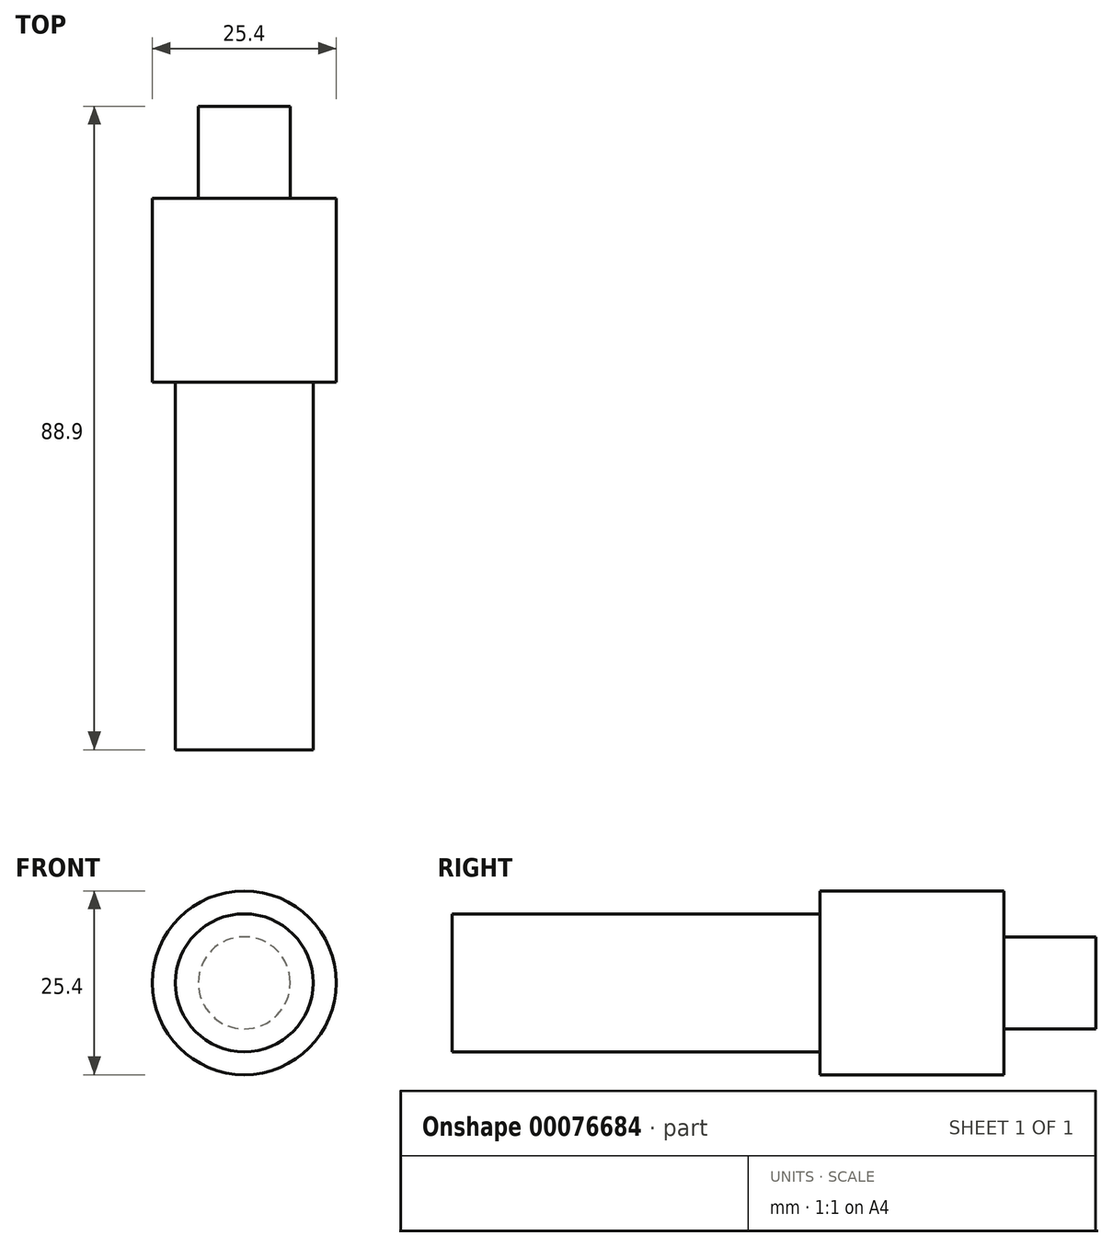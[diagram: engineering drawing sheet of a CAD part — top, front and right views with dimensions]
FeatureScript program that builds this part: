
annotation { "Feature Type Name" : "Feature", "Feature Type Description" : "" }
export const myFeature = defineFeature(function(context is Context, id is Id, definition is map)
    precondition{}
    {
        {
            var Q0;
            Q0=qCreatedBy(makeId("Front.planeOp"),FACE);
            var sketch = newSketch(context, id + "F0", { "sketchPlane" : qUnion([Q0])});
            skCircle(sketch, "E0", {"center": v(0, 0) * mm, "radius": 12.7 * mm});
            skSolve(sketch);
        }
        {
            var Q0;
            Q0=makeQuery(id+"F0.imprint","IMPRINT",FACE,{"disambiguationData":[TD([[makeQuery(id+"F0.imprint","IMPRINT",EDGE,{"derivedFrom":sQuery(id+"F0.wireOp",EDGE,"E0")}),1.0]])]});
            extrude(context, id + "F1", {"entities" : qUnion([Q0]), "depth" : 25.4 * mm});
        }
        {
            var Q0;
            Q0=makeQuery(id+"F1.opExtrude","CAP_FACE",FACE,{"disambiguationData":[OSD([sQuery(id+"F0.wireOp",EDGE,"E0")])],"isStart":true});
            var sketch = newSketch(context, id + "F2", { "sketchPlane" : qUnion([Q0])});
            skCircle(sketch, "E1", {"center": v(0, 0) * mm, "radius": 6.35 * mm});
            skSolve(sketch);
        }
        {
            var Q0;
            Q0=makeQuery(id+"F2.imprint","IMPRINT",FACE,{"disambiguationData":[TD([[makeQuery(id+"F2.imprint","IMPRINT",EDGE,{"derivedFrom":sQuery(id+"F2.wireOp",EDGE,"E1")}),1.0]])]});
            extrude(context, id + "F3", {"entities" : qUnion([Q0]), "operationType" : NewBodyOperationType.ADD, "depth" : 12.7 * mm});
        }
        {
            var Q0;
            Q0=makeQuery(id+"F1.opExtrude","CAP_FACE",FACE,{"disambiguationData":[OSD([sQuery(id+"F0.wireOp",EDGE,"E0")])],"isStart":false});
            var sketch = newSketch(context, id + "F4", { "sketchPlane" : qUnion([Q0])});
            skCircle(sketch, "E2", {"center": v(0, 0) * mm, "radius": 9.53 * mm});
            skSolve(sketch);
        }
        {
            var Q0;
            Q0=makeQuery(id+"F4.imprint","IMPRINT",FACE,{"disambiguationData":[TD([[makeQuery(id+"F4.imprint","IMPRINT",EDGE,{"derivedFrom":sQuery(id+"F4.wireOp",EDGE,"E2")}),1.0]])]});
            extrude(context, id + "F5", {"entities" : qUnion([Q0]), "operationType" : NewBodyOperationType.ADD, "depth" : 50.8 * mm});
        }
    });
